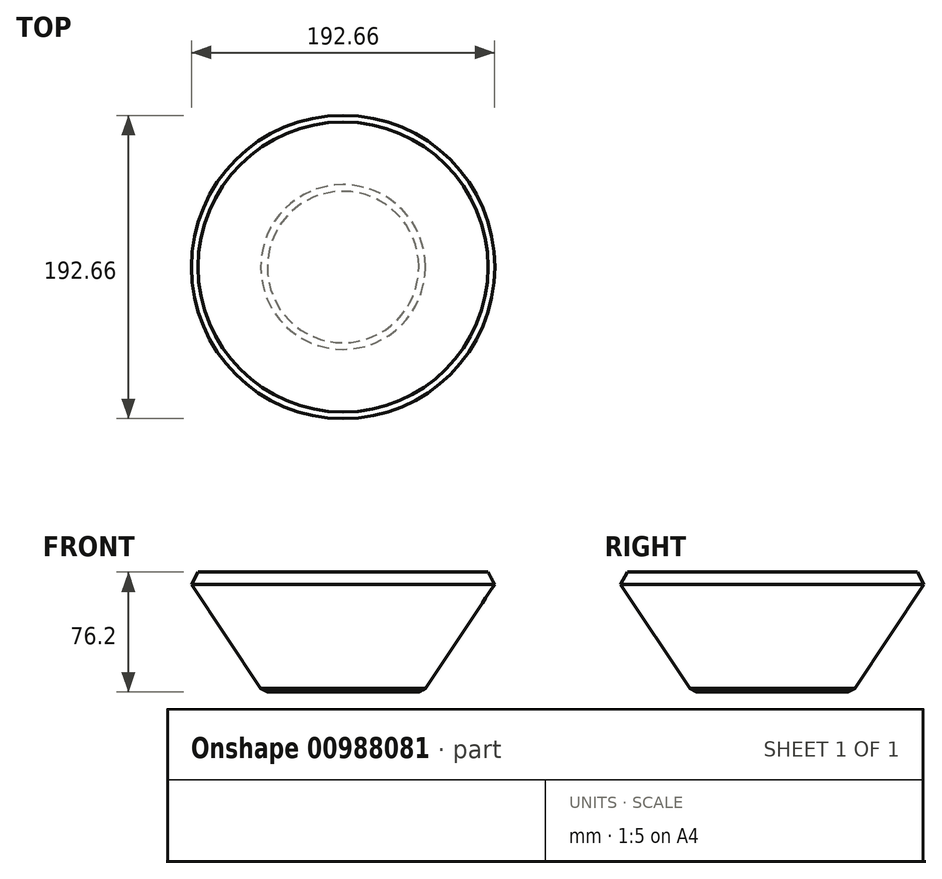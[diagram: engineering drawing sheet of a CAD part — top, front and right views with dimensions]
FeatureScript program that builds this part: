
annotation { "Feature Type Name" : "Feature", "Feature Type Description" : "" }
export const myFeature = defineFeature(function(context is Context, id is Id, definition is map)
    precondition{}
    {
        {
            var Q0;
            Q0=qCreatedBy(makeId("Top.planeOp"),FACE);
            var sketch = newSketch(context, id + "F0", { "sketchPlane" : qUnion([Q0])});
            skCircle(sketch, "E0", {"center": v(0, 0) * mm, "radius": 101.6 * mm});
            skSolve(sketch);
        }
        {
            var Q0;
            Q0=qCreatedBy(makeId("Top.planeOp"),FACE);
            cPlane(context, id + "F1", {"entities" : qUnion([Q0]), "cplaneType" : CPlaneType.OFFSET, "offset" : 76.2 * mm, "oppositeDirection" : true, "width" : 152.4 * mm, "height" : 152.4 * mm});
        }
        {
            var Q0;
            Q0=qCreatedBy(id+"F1.planeOp",FACE);
            var sketch = newSketch(context, id + "F2", { "sketchPlane" : qUnion([Q0])});
            skCircle(sketch, "E1", {"center": v(0, 0) * mm, "radius": 50.8 * mm});
            skSolve(sketch);
        }
        {
            var Q0;
            Q0=makeQuery(id+"F0.imprint","IMPRINT",FACE,{"disambiguationData":[TD([[makeQuery(id+"F0.imprint","IMPRINT",EDGE,{"derivedFrom":sQuery(id+"F0.wireOp",EDGE,"E0")}),1.0]])]});
            var Q1;
            Q1=makeQuery(id+"F2.imprint","IMPRINT",FACE,{"disambiguationData":[TD([[makeQuery(id+"F2.imprint","IMPRINT",EDGE,{"derivedFrom":sQuery(id+"F2.wireOp",EDGE,"E1")}),1.0]])]});
            loft(context, id + "F3", {"sheetProfilesArray" : [{ "sheetProfileEntities" : qUnion([Q0]) }, { "sheetProfileEntities" : qUnion([Q1]) }]});
        }
        {
            var Q0;
            Q0=makeQuery(id+"F3.opLoft","MID_CAP_EDGE",EDGE,{"disambiguationData":[OSD([sQuery(id+"F0.wireOp",EDGE,"E0")])],"capPos":0.0});
            var Q1;
            Q1=makeQuery(id+"F3.opLoft","MID_CAP_EDGE",EDGE,{"disambiguationData":[OSD([sQuery(id+"F2.wireOp",EDGE,"E1")])],"capPos":1.0});
            chamfer(context, id + "F4", {"entities" : qUnion([Q0, Q1]), "width" : 5.08 * mm, "tangentPropagation" : true});
        }
    });
